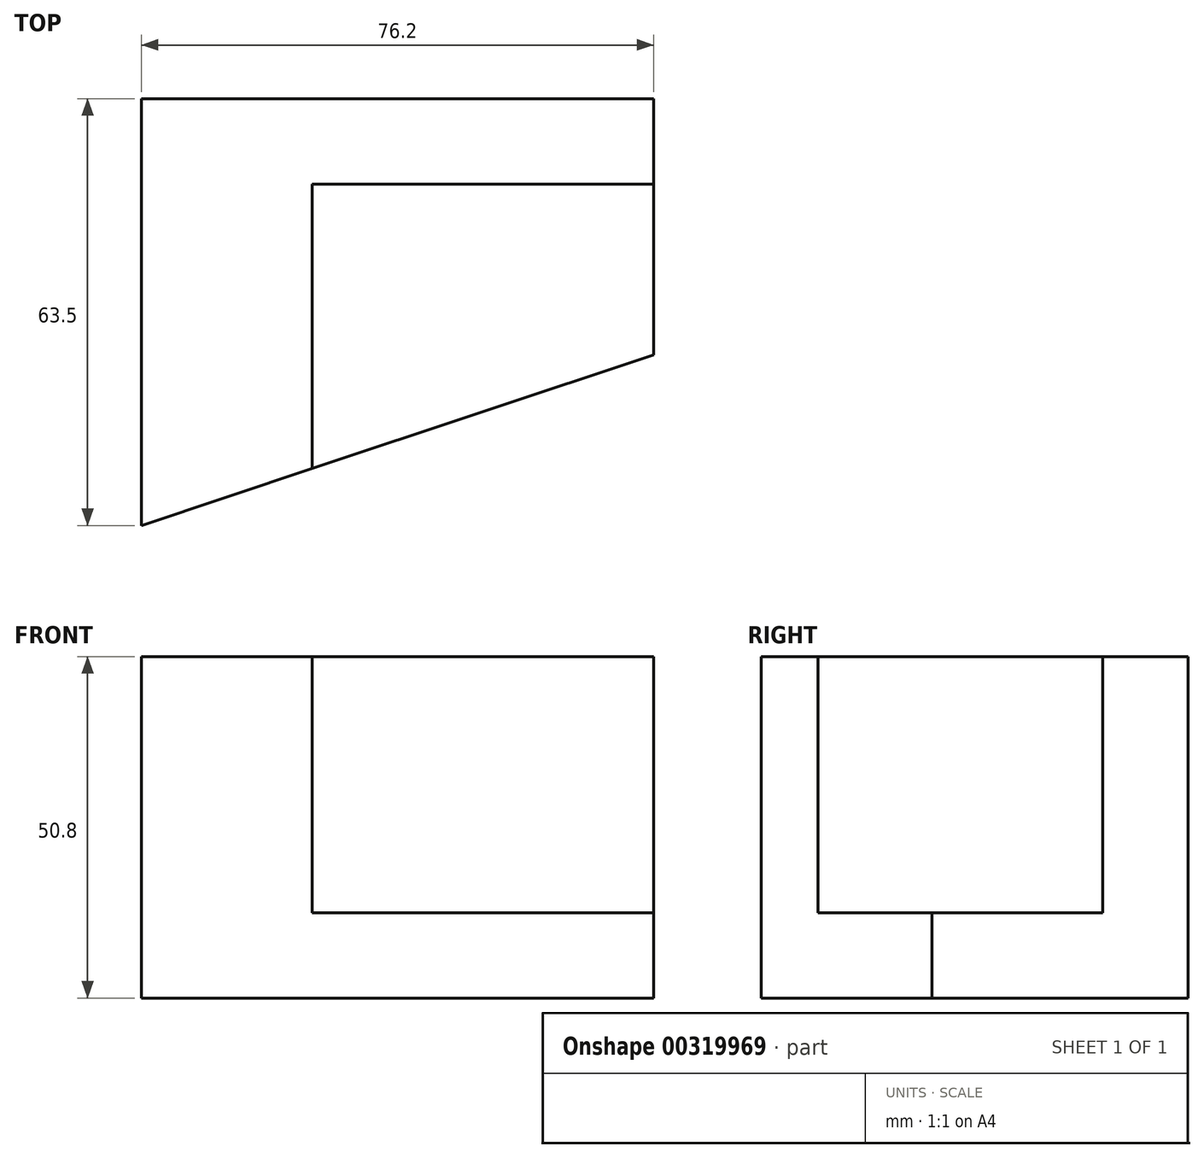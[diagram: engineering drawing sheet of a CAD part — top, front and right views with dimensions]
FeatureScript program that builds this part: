
annotation { "Feature Type Name" : "Feature", "Feature Type Description" : "" }
export const myFeature = defineFeature(function(context is Context, id is Id, definition is map)
    precondition{}
    {
        {
            var Q0;
            Q0=qCreatedBy(makeId("Top.planeOp"),FACE);
            var sketch = newSketch(context, id + "F0", { "sketchPlane" : qUnion([Q0])});
            skLineSegment(sketch, "E0.top", {"start": v(38.1, 31.75) * mm, "end": v(-38.1, 31.75) * mm});
            skLineSegment(sketch, "E0.right", {"start": v(-38.1, -31.75) * mm, "end": v(-38.1, 31.75) * mm});
            skPoint(sketch, "E0.middle", {"position": v(0, 0) * mm});
            skLineSegment(sketch, "E1", {"start": v(-38.1, -31.75) * mm, "end": v(38.1, -6.35) * mm});
            skLineSegment(sketch, "E2", {"start": v(38.1, 31.75) * mm, "end": v(38.1, -6.35) * mm});
            skSolve(sketch);
        }
        {
            var Q0;
            Q0=makeQuery(id+"F0.imprint","IMPRINT",FACE,{"disambiguationData":[TD([[makeQuery(id+"F0.imprint","IMPRINT",EDGE,{"derivedFrom":sQuery(id+"F0.wireOp",EDGE,"E0.top")}),1.0]])]});
            extrude(context, id + "F1", {"entities" : qUnion([Q0]), "depth" : 50.8 * mm});
        }
        {
            var Q0;
            Q0=makeQuery(id+"F1.opExtrude","CAP_FACE",FACE,{"disambiguationData":[OSD([sQuery(id+"F0.wireOp",EDGE,"E0.top"),sQuery(id+"F0.wireOp",EDGE,"E0.right"),sQuery(id+"F0.wireOp",EDGE,"E1"),sQuery(id+"F0.wireOp",EDGE,"E2")])],"isStart":false});
            var sketch = newSketch(context, id + "F2", { "sketchPlane" : qUnion([Q0])});
            skLineSegment(sketch, "E3", {"start": v(38.1, 19.05) * mm, "end": v(-12.7, 19.05) * mm});
            skLineSegment(sketch, "E4", {"start": v(-12.7, 19.05) * mm, "end": v(-12.7, -23.28) * mm});
            skSolve(sketch);
        }
        {
            var Q0;
            {var subQ0=sQuery(id+"F2.wireOp",EDGE,"E3");Q0=makeQuery(id+"F2.imprint","IMPRINT",FACE,{"disambiguationData":[TD([[makeQuery(id+"F2.imprint","IMPRINT",EDGE,{"derivedFrom":subQ0}),1.0]])]});}
            extrude(context, id + "F3", {"entities" : qUnion([Q0]), "operationType" : NewBodyOperationType.REMOVE, "oppositeDirection" : true, "depth" : 38.1 * mm});
        }
    });
